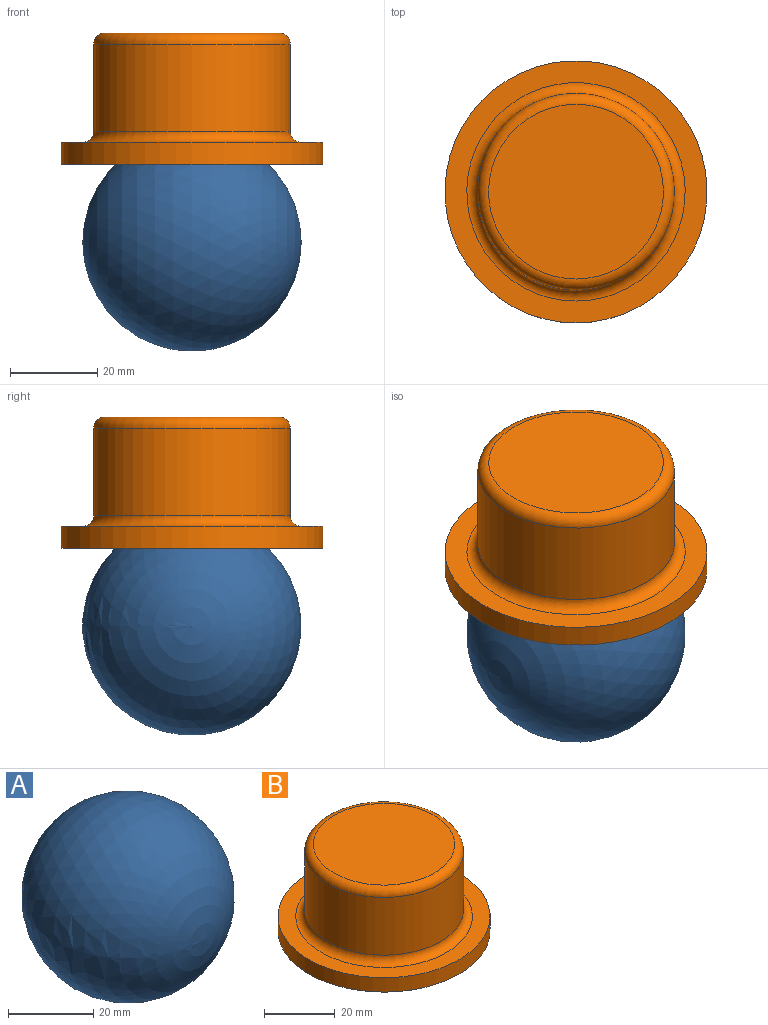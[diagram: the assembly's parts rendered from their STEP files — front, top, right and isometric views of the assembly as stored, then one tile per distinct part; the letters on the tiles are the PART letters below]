
ASSEMBLY  parts=2 mates=1
PART A: 1 faces, bbox 50x50x50 mm
  f0: sphere r=25mm, area 7854mm2
PART B: 9 faces, bbox 60x60x30 mm
  f0: cylinder r=17.5mm len=35mm, axis (0,0,-1), area 2968.8mm2, adj f3,f6
  f1: cylinder r=30mm len=60mm, axis (0,0,-1), area 942.5mm2, adj f2,f3
  f2: plane 60x60mm, normal (0,0,1), area 863.9mm2, adj f1,f7
  f3: plane 60x60mm, normal (0,0,-1), area 1865.3mm2, adj f0,f1
  f4: plane 40x40mm, normal (0,0,1), area 1256.6mm2, adj f8
  f5: cylinder r=22.5mm len=45mm, axis (0,0,-1), area 2827.4mm2, adj f7,f8
  f6: plane 35x35mm, normal (0,0,-1), area 962.1mm2, adj f0
  f7: torus R=25mm, axis (0,0,1), area 577.6mm2, adj f2,f5
  f8: torus R=20mm, axis (0,0,1), area 532.8mm2, adj f4,f5
PLACE A rot(axis=(0,0,-1),90deg) t=(0,0,0)mm
PLACE B rot(axis=(0,0,-1),90deg) t=(0,0,17.85)mm
MATE slider B.f0 <-> A.f0  axis (0,0,-1) through (0,0,17.85)mm
